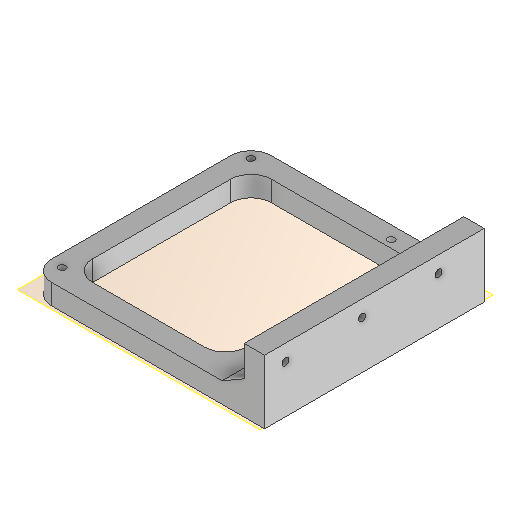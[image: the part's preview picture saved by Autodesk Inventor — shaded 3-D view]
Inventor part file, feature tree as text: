
AUTODESK INVENTOR PART (.ipt)
format: ipt  version: 2024.1 (Build 281209000, 209)  size: 252,928 bytes
history: native  units: mm
features: reference x4, sketch x3, other x3, extrude x2, plane x1, chamfer x1, fillet x1, hole x1
ambient origin geometry x8: Origin, YZ Plane, XZ Plane, XY Plane, X Axis, Y Axis, Z Axis, Center Point
bodies: Volumenkörper1 (feature_tree)
feature tree (16):
  plane  "Arbeitsebene1"
  extrude  "Extrusion1"  Depth=8.0mm
  extrude  "Extrusion2"  Depth=2.8mm
  chamfer  "Fasen1"  Distance=8.0mm
  fillet  "Rundung1"  Radius=17.0mm
  hole  "Bohrung1"  [1 undecoded]
  sketch  "Skizze1"  dims[d0=8.0mm d1=2.8mm]
  reference  "Referenz1"
  reference  "Referenz2"
  sketch  "Skizze2"  dims[d2=2.8mm d3=2.8mm]
  reference  "Referenz3"
  sketch  "Skizze3"  dims[d4=2.8mm d5=8.0mm d6=0.0mm d7=17.0mm d8=8.0mm d9=0.0mm d10=5.0mm d11=2.0mm d12=60.0deg d13=8.0mm d14=2.8mm d15=6.0mm d16=4.0mm d17=2.0mm d18=90.0deg d19=20.0mm d20=0.0mm]
  reference  "Referenz4"
  other  "Assembly_Planktoscope_Uc2version_wormdrive_V3.iam"
  other  "00_UC2_ESP32-cnc_v3:1"
  other  "60_Planktoscope_MicroscopeHolder_Bottom_v0:1"
note: 1 required parameter value undecoded (feature->parameter linkage not recoverable at this tier; creation-order binding heuristic only, values carry confidence <= 0.55)
